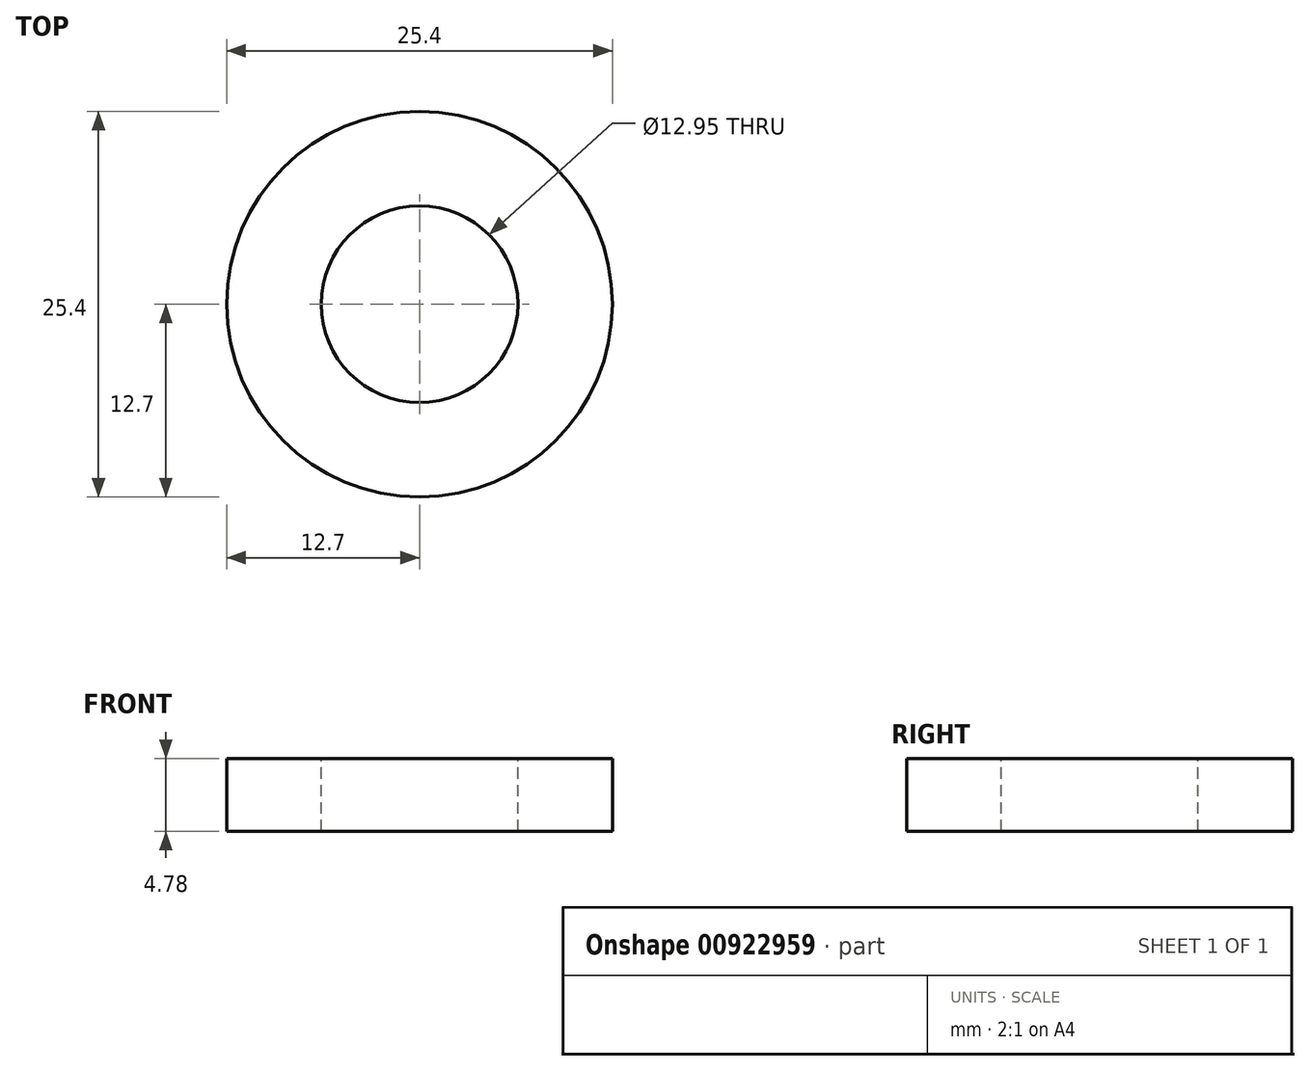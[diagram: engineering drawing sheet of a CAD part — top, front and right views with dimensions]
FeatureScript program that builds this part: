
annotation { "Feature Type Name" : "Feature", "Feature Type Description" : "" }
export const myFeature = defineFeature(function(context is Context, id is Id, definition is map)
    precondition{}
    {
        {
            var Q0;
            Q0=qCreatedBy(makeId("Front.planeOp"),FACE);
            var sketch = newSketch(context, id + "F0", { "sketchPlane" : qUnion([Q0])});
            skLineSegment(sketch, "E0.bottom", {"start": v(6.48, 0) * mm, "end": v(12.7, 0) * mm});
            skLineSegment(sketch, "E0.top", {"start": v(6.48, -4.78) * mm, "end": v(12.7, -4.78) * mm});
            skLineSegment(sketch, "E0.left", {"start": v(6.48, 0) * mm, "end": v(6.48, -4.78) * mm});
            skLineSegment(sketch, "E0.right", {"start": v(12.7, 0) * mm, "end": v(12.7, -4.78) * mm});
            skLineSegment(sketch, "E1", {"start": v(0, 10.24) * mm, "end": v(0, -11.18) * mm, "construction": true});
            skSolve(sketch);
        }
        {
            var Q0;
            Q0 = qSketchRegion(id + "F0", true);
            var Q1;
            Q1=sQuery(id+"F0.wireOp",EDGE,"E1");
            revolve(context, id + "F1", {"surfaceOperationType" : NewSurfaceOperationType.NEW, "entities" : qUnion([Q0]), "axis" : qUnion([Q1]), "revolveType" : RevolveType.FULL});
        }
    });
